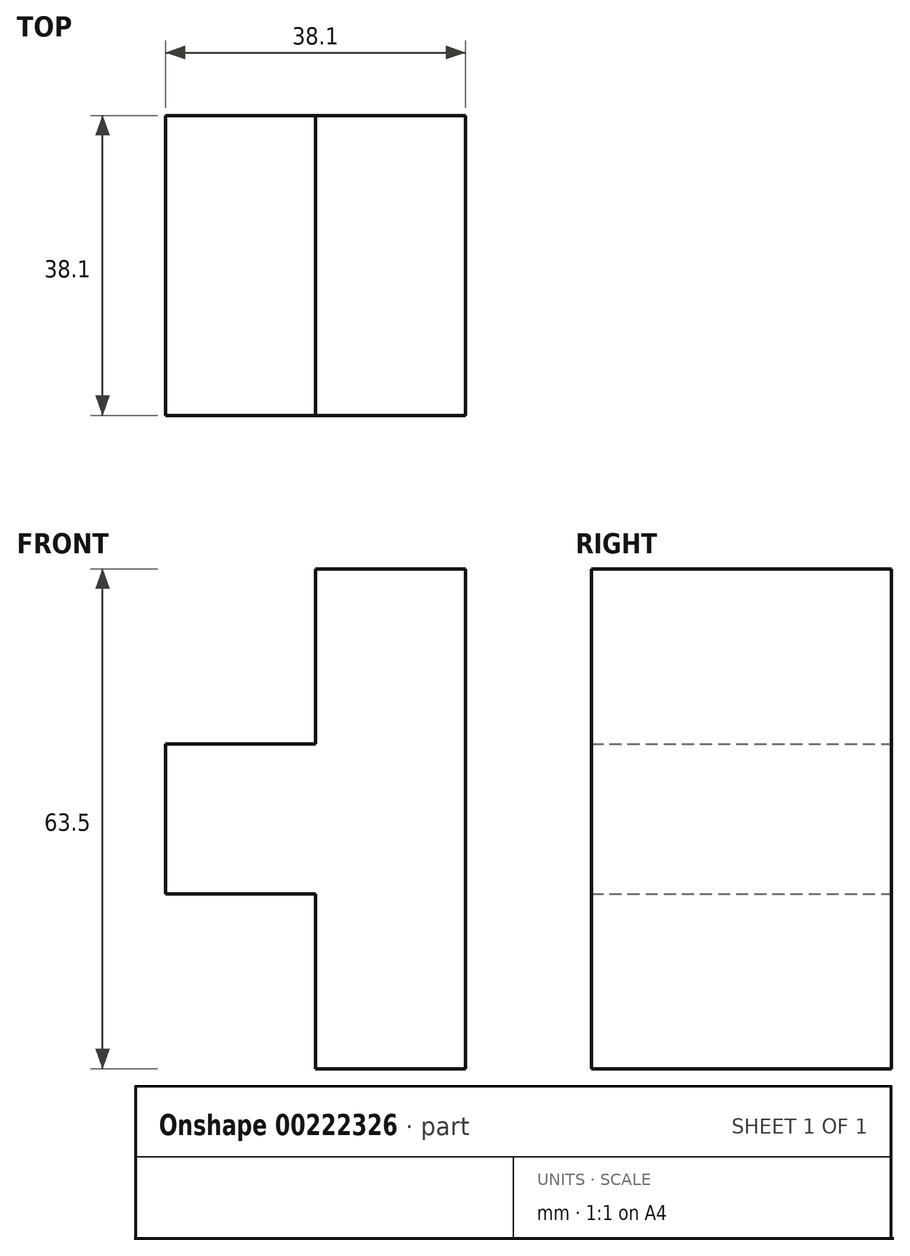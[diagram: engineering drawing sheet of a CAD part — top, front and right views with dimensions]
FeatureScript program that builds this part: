
annotation { "Feature Type Name" : "Feature", "Feature Type Description" : "" }
export const myFeature = defineFeature(function(context is Context, id is Id, definition is map)
    precondition{}
    {
        {
            var Q0;
            Q0=qCreatedBy(makeId("Front.planeOp"),FACE);
            var sketch = newSketch(context, id + "F0", { "sketchPlane" : qUnion([Q0])});
            skLineSegment(sketch, "E0.bottom", {"start": v(-37.77, 7.58) * mm, "end": v(-56.82, 7.58) * mm});
            skLineSegment(sketch, "E0.top", {"start": v(-37.77, 71.08) * mm, "end": v(-56.82, 71.08) * mm});
            skLineSegment(sketch, "E0.left", {"start": v(-37.77, 7.58) * mm, "end": v(-37.77, 71.08) * mm});
            skLineSegment(sketch, "E0.right", {"start": v(-56.82, 7.58) * mm, "end": v(-56.82, 71.08) * mm});
            skPoint(sketch, "E0.middle", {"position": v(-47.3, 39.33) * mm});
            skLineSegment(sketch, "E1.bottom", {"start": v(-56.82, 29.8) * mm, "end": v(-75.87, 29.8) * mm});
            skLineSegment(sketch, "E1.top", {"start": v(-56.82, 48.86) * mm, "end": v(-75.87, 48.86) * mm});
            skLineSegment(sketch, "E1.left", {"start": v(-56.82, 29.8) * mm, "end": v(-56.82, 48.86) * mm});
            skLineSegment(sketch, "E1.right", {"start": v(-75.87, 29.8) * mm, "end": v(-75.87, 48.86) * mm});
            skPoint(sketch, "E1.middle", {"position": v(-66.35, 39.33) * mm});
            skPoint(sketch, "E2.endSnap0", {"position": v(-56.82, 39.33) * mm});
            skSolve(sketch);
        }
        {
            var Q0;
            Q0 = qSketchRegion(id + "F0", true);
            extrude(context, id + "F1", {"entities" : qUnion([Q0]), "depth" : 25.4 * mm});
        }
        {
            var Q0;
            Q0 = qSketchRegion(id + "F0", true);
            extrude(context, id + "F2", {"entities" : qUnion([Q0]), "operationType" : NewBodyOperationType.ADD, "endBound" : BoundingType.SYMMETRIC, "depth" : 25.4 * mm});
        }
    });
